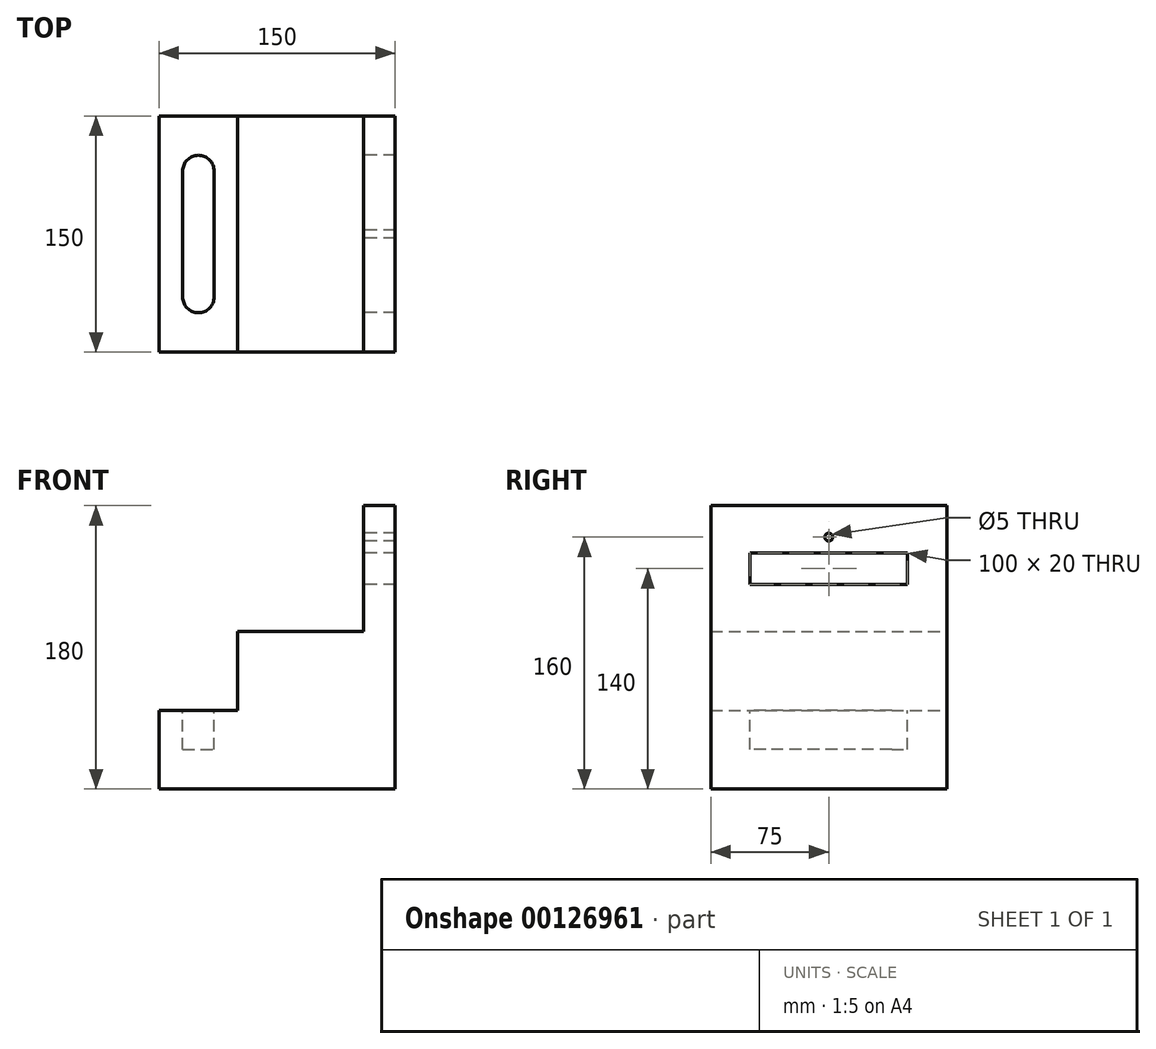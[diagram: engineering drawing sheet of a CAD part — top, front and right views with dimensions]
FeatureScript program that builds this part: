
annotation { "Feature Type Name" : "Feature", "Feature Type Description" : "" }
export const myFeature = defineFeature(function(context is Context, id is Id, definition is map)
    precondition{}
    {
        {
            var Q0;
            Q0=qCreatedBy(makeId("Front.planeOp"),FACE);
            var sketch = newSketch(context, id + "F0", { "sketchPlane" : qUnion([Q0])});
            skLineSegment(sketch, "E0.bottom", {"start": v(75, 90) * mm, "end": v(55, 90) * mm});
            skLineSegment(sketch, "E0.top", {"start": v(75, -90) * mm, "end": v(-75, -90) * mm});
            skLineSegment(sketch, "E0.left", {"start": v(75, 90) * mm, "end": v(75, -90) * mm});
            skLineSegment(sketch, "E0.right", {"start": v(-75, -40) * mm, "end": v(-75, -90) * mm});
            skPoint(sketch, "E0.middle", {"position": v(0, 0) * mm});
            skLineSegment(sketch, "E1", {"start": v(-75, -90) * mm, "end": v(-75, -40) * mm});
            skLineSegment(sketch, "E2", {"start": v(-75, -40) * mm, "end": v(-25, -40) * mm});
            skLineSegment(sketch, "E3", {"start": v(-25, -40) * mm, "end": v(-25, 10) * mm});
            skLineSegment(sketch, "E4", {"start": v(-25, 10) * mm, "end": v(55, 10) * mm});
            skLineSegment(sketch, "E5", {"start": v(55, 10) * mm, "end": v(55, 90) * mm});
            skLineSegment(sketch, "E6", {"start": v(55, 90) * mm, "end": v(75, 90) * mm});
            skPoint(sketch, "E7.orphan", {"position": v(-75, 90) * mm});
            skSolve(sketch);
        }
        {
            var Q0;
            Q0 = qSketchRegion(id + "F0", true);
            extrude(context, id + "F1", {"entities" : qUnion([Q0]), "depth" : 150 * mm});
        }
        {
            var Q0;
            Q0=makeQuery(id+"F1.opExtrude","SWEPT_FACE",FACE,{"disambiguationData":[OSD([sQuery(id+"F0.wireOp",EDGE,"E5")])]});
            var sketch = newSketch(context, id + "F2", { "sketchPlane" : qUnion([Q0])});
            skLineSegment(sketch, "E8.bottom", {"start": v(125, 60) * mm, "end": v(25, 60) * mm});
            skLineSegment(sketch, "E8.top", {"start": v(125, 40) * mm, "end": v(25, 40) * mm});
            skLineSegment(sketch, "E8.left", {"start": v(125, 60) * mm, "end": v(125, 40) * mm});
            skLineSegment(sketch, "E8.right", {"start": v(25, 60) * mm, "end": v(25, 40) * mm});
            skSolve(sketch);
        }
        {
            var Q0;
            Q0 = qSketchRegion(id + "F2", true);
            extrude(context, id + "F3", {"entities" : qUnion([Q0]), "operationType" : NewBodyOperationType.REMOVE, "endBound" : BoundingType.THROUGH_ALL, "oppositeDirection" : true, "depth" : 25.4 * mm});
        }
        {
            var Q0;
            Q0=makeQuery(id+"F1.opExtrude","SWEPT_FACE",FACE,{"disambiguationData":[OSD([sQuery(id+"F0.wireOp",EDGE,"E5")])]});
            var sketch = newSketch(context, id + "F4", { "sketchPlane" : qUnion([Q0])});
            skCircle(sketch, "E9", {"center": v(75, 70) * mm, "radius": 2.5 * mm});
            skPoint(sketch, "E9.centerSnap0", {"position": v(75, 60) * mm});
            skSolve(sketch);
        }
        {
            var Q0;
            Q0=makeQuery(id+"F1.opExtrude","SWEPT_FACE",FACE,{"disambiguationData":[OSD([sQuery(id+"F0.wireOp",EDGE,"E2")])]});
            var sketch = newSketch(context, id + "F5", { "sketchPlane" : qUnion([Q0])});
            skLineSegment(sketch, "E10.left", {"start": v(-60, -35) * mm, "end": v(-60, -115) * mm});
            skLineSegment(sketch, "E10.right", {"start": v(-40, -35) * mm, "end": v(-40, -115) * mm});
            skArc(sketch, "E11", {"start": v(-60, -115) * mm, "mid": v(-50, -125) * mm, "end": v(-40, -115) * mm});
            skArc(sketch, "E12", {"start": v(-40, -35) * mm, "mid": v(-50, -25) * mm, "end": v(-60, -35) * mm});
            skSolve(sketch);
        }
        {
            var Q0;
            Q0 = qSketchRegion(id + "F5", true);
            extrude(context, id + "F6", {"entities" : qUnion([Q0]), "operationType" : NewBodyOperationType.REMOVE, "oppositeDirection" : true, "depth" : 25 * mm});
        }
        {
            var Q0;
            Q0=makeQuery(id+"F4.imprint","IMPRINT",FACE,{"disambiguationData":[TD([[makeQuery(id+"F4.imprint","IMPRINT",EDGE,{"derivedFrom":sQuery(id+"F4.wireOp",EDGE,"E9")}),1.0]])]});
            extrude(context, id + "F7", {"entities" : qUnion([Q0]), "operationType" : NewBodyOperationType.REMOVE, "endBound" : BoundingType.THROUGH_ALL, "oppositeDirection" : true, "depth" : 25.4 * mm});
        }
    });
